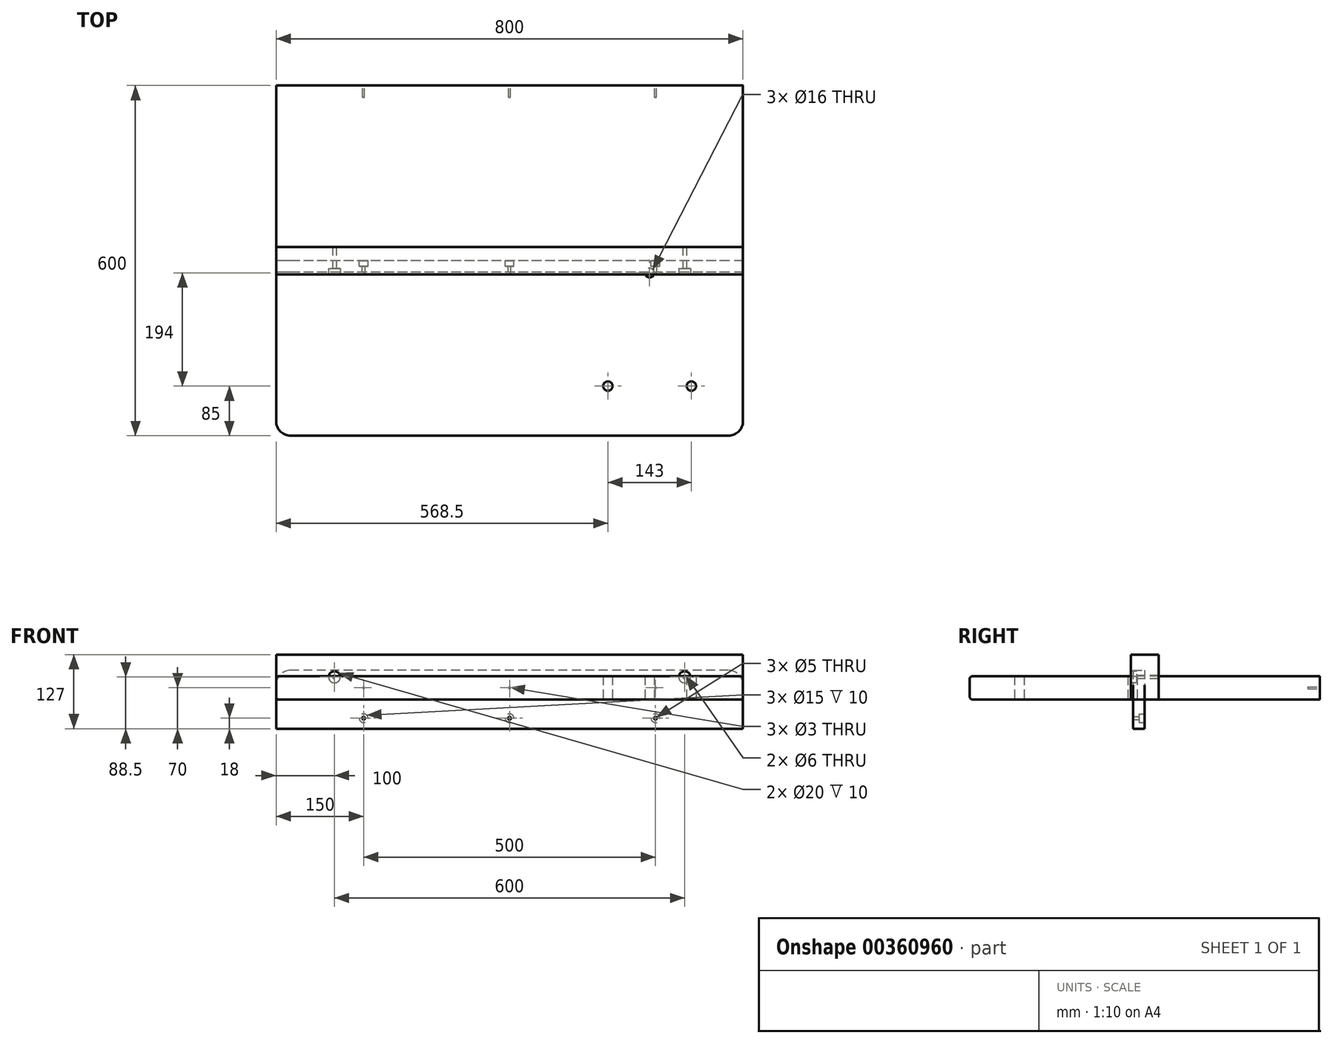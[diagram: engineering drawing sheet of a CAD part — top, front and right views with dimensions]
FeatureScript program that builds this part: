
annotation { "Feature Type Name" : "Feature", "Feature Type Description" : "" }
export const myFeature = defineFeature(function(context is Context, id is Id, definition is map)
    precondition{}
    {
        {
            var Q0;
            Q0=qCreatedBy(makeId("Top.planeOp"),FACE);
            var sketch = newSketch(context, id + "F0", { "sketchPlane" : qUnion([Q0])});
            skLineSegment(sketch, "E0.bottom", {"start": v(400, 300) * mm, "end": v(-400, 300) * mm});
            skLineSegment(sketch, "E0.top", {"start": v(400, -300) * mm, "end": v(-400, -300) * mm});
            skLineSegment(sketch, "E0.left", {"start": v(400, 300) * mm, "end": v(400, -300) * mm});
            skLineSegment(sketch, "E0.right", {"start": v(-400, 300) * mm, "end": v(-400, -300) * mm});
            skPoint(sketch, "E0.middle", {"position": v(0, 0) * mm});
            skPoint(sketch, "E1", {"position": v(240, -21) * mm});
            skPoint(sketch, "E2", {"position": v(168.5, -215) * mm});
            skPoint(sketch, "E3", {"position": v(311.5, -215) * mm});
            skLineSegment(sketch, "E4", {"start": v(311.5, -215) * mm, "end": v(168.5, -215) * mm, "construction": true});
            skLineSegment(sketch, "E5", {"start": v(240, -21) * mm, "end": v(240, -215) * mm, "construction": true});
            skSolve(sketch);
        }
        {
            var Q0;
            Q0=makeQuery(id+"F0.imprint","IMPRINT",FACE,{"disambiguationData":[TD([[makeQuery(id+"F0.imprint","IMPRINT",EDGE,{"derivedFrom":sQuery(id+"F0.wireOp",EDGE,"E0.bottom")}),1.0]])]});
            extrude(context, id + "F1", {"entities" : qUnion([Q0]), "depth" : 40 * mm, "offsetDistance" : 25 * mm});
        }
        {
            var Q0;
            Q0=makeQuery(id+"F1.opExtrude","SWEPT_EDGE",EDGE,{"disambiguationData":[OSD([sQuery(id+"F0.wireOp",EDGE,"E0.top"),sQuery(id+"F0.wireOp",EDGE,"E0.left")])]});
            var Q1;
            Q1=makeQuery(id+"F1.opExtrude","SWEPT_EDGE",EDGE,{"disambiguationData":[OSD([sQuery(id+"F0.wireOp",EDGE,"E0.top"),sQuery(id+"F0.wireOp",EDGE,"E0.right")])]});
            fillet(context, id + "F2", {"entities" : qUnion([Q0, Q1]), "radius" : 25 * mm, "tangentPropagation" : true, "allowEdgeOverflow" : false});
        }
        {
            var Q0;
            Q0=makeQuery(id+"F1.opExtrude","CAP_EDGE",EDGE,{"disambiguationData":[OSD([sQuery(id+"F0.wireOp",EDGE,"E0.left")])],"isStart":false});
            var Q1;
            Q1=makeQuery(id+"F1.opExtrude","CAP_EDGE",EDGE,{"disambiguationData":[OSD([sQuery(id+"F0.wireOp",EDGE,"E0.top")])],"isStart":true});
            fillet(context, id + "F3", {"entities" : qUnion([Q0, Q1]), "radius" : 5 * mm, "tangentPropagation" : true, "allowEdgeOverflow" : false});
        }
        {
            var Q0;
            Q0=makeQuery(id+"F1.opExtrude","SWEPT_FACE",FACE,{"disambiguationData":[OSD([sQuery(id+"F0.wireOp",EDGE,"E0.bottom")])]});
            var sketch = newSketch(context, id + "F4", { "sketchPlane" : qUnion([Q0])});
            skLineSegment(sketch, "E6", {"start": v(-400, 20) * mm, "end": v(400, 20) * mm, "construction": true});
            skPoint(sketch, "E7", {"position": v(0, 20) * mm});
            skPoint(sketch, "E8", {"position": v(-250, 20) * mm});
            skPoint(sketch, "E9", {"position": v(250, 20) * mm});
            skSolve(sketch);
        }
        {
            var Q0;
            Q0=sQuery(id+"F4.wireOp",VERTEX,"E8");
            var Q1;
            Q1=sQuery(id+"F4.wireOp",VERTEX,"E7");
            var Q2;
            Q2=sQuery(id+"F4.wireOp",VERTEX,"E9");
            var Q3;
            Q3=makeQuery(id+"F1.opExtrude","SWEPT_BODY",BODY,{"disambiguationData":[OSD([sQuery(id+"F0.wireOp",EDGE,"E0.bottom"),sQuery(id+"F0.wireOp",EDGE,"E0.top"),sQuery(id+"F0.wireOp",EDGE,"E0.left"),sQuery(id+"F0.wireOp",EDGE,"E0.right")])]});
            hole(context, id + "F5", {"style" : HoleStyle.SIMPLE, "endStyle" : HoleEndStyle.BLIND, "holeDiameter" : 3 * mm, "holeDepth" : 20 * mm, "isTappedThrough" : true, "tappedDepth" : 12 * mm, "tapClearance" : 3, "locations" : qUnion([Q0, Q1, Q2]), "scope" : qUnion([Q3])});
        }
        {
            var Q0;
            Q0=qCreatedBy(makeId("Front.planeOp"),FACE);
            var sketch = newSketch(context, id + "F6", { "sketchPlane" : qUnion([Q0])});
            skLineSegment(sketch, "E10.bottom", {"start": v(375, 50) * mm, "end": v(-375, 50) * mm});
            skLineSegment(sketch, "E10.top", {"start": v(400, -50) * mm, "end": v(-400, -50) * mm});
            skLineSegment(sketch, "E10.left", {"start": v(400, 25) * mm, "end": v(400, -50) * mm});
            skLineSegment(sketch, "E10.right", {"start": v(-400, 25) * mm, "end": v(-400, -50) * mm});
            skPoint(sketch, "E10.middle", {"position": v(0, 0) * mm});
            skLineSegment(sketch, "E11", {"start": v(-400, -32) * mm, "end": v(400, -32) * mm, "construction": true});
            skPoint(sketch, "E11.endSnap0", {"position": v(400, 0) * mm});
            skPoint(sketch, "E12", {"position": v(0, -32) * mm});
            skPoint(sketch, "E13", {"position": v(250, -32) * mm});
            skPoint(sketch, "E14", {"position": v(-250, -32) * mm});
            skPoint(sketch, "E15.visualSharp", {"position": v(-400, 50) * mm});
            skArc(sketch, "E15.filletArc", {"start": v(-375, 50) * mm, "mid": v(-392.68, 42.68) * mm, "end": v(-400, 25) * mm});
            skPoint(sketch, "E16.visualSharp", {"position": v(400, 50) * mm});
            skArc(sketch, "E16.filletArc", {"start": v(400, 25) * mm, "mid": v(392.68, 42.68) * mm, "end": v(375, 50) * mm});
            skSolve(sketch);
        }
        {
            var Q0;
            Q0=makeQuery(id+"F6.imprint","IMPRINT",FACE,{"disambiguationData":[TD([[makeQuery(id+"F6.imprint","IMPRINT",EDGE,{"derivedFrom":sQuery(id+"F6.wireOp",EDGE,"E10.bottom")}),1.0]])]});
            extrude(context, id + "F7", {"entities" : qUnion([Q0]), "depth" : 20 * mm});
        }
        {
            var Q0;
            Q0=sQuery(id+"F6.wireOp",VERTEX,"E13");
            var Q1;
            Q1=sQuery(id+"F6.wireOp",VERTEX,"E12");
            var Q2;
            Q2=sQuery(id+"F6.wireOp",VERTEX,"E14");
            var Q3;
            Q3=makeQuery(id+"F7.opExtrude","SWEPT_BODY",BODY,{"disambiguationData":[OSD([sQuery(id+"F6.wireOp",EDGE,"E10.bottom"),sQuery(id+"F6.wireOp",EDGE,"E10.top"),sQuery(id+"F6.wireOp",EDGE,"E10.left"),sQuery(id+"F6.wireOp",EDGE,"E10.right"),sQuery(id+"F6.wireOp",EDGE,"E15.filletArc"),sQuery(id+"F6.wireOp",EDGE,"E16.filletArc")])]});
            hole(context, id + "F8", {"style" : HoleStyle.C_BORE, "endStyle" : HoleEndStyle.THROUGH, "oppositeDirection" : true, "holeDiameter" : 5 * mm, "cBoreDiameter" : 15 * mm, "cBoreDepth" : 10 * mm, "isTappedThrough" : true, "tappedDepth" : 12 * mm, "tapClearance" : 3, "locations" : qUnion([Q0, Q1, Q2]), "scope" : qUnion([Q3])});
        }
        {
            var Q0;
            Q0=qCreatedBy(makeId("Top.planeOp"),FACE);
            var sketch = newSketch(context, id + "F9", { "sketchPlane" : qUnion([Q0])});
            skLineSegment(sketch, "E17.bottom", {"start": v(400, 23.5) * mm, "end": v(-400, 23.5) * mm});
            skLineSegment(sketch, "E17.top", {"start": v(400, -23.5) * mm, "end": v(-400, -23.5) * mm});
            skLineSegment(sketch, "E17.left", {"start": v(400, 23.5) * mm, "end": v(400, -23.5) * mm});
            skLineSegment(sketch, "E17.right", {"start": v(-400, 23.5) * mm, "end": v(-400, -23.5) * mm});
            skPoint(sketch, "E17.middle", {"position": v(0, 0) * mm});
            skSolve(sketch);
        }
        {
            var Q0;
            Q0=makeQuery(id+"F9.imprint","IMPRINT",FACE,{"disambiguationData":[TD([[makeQuery(id+"F9.imprint","IMPRINT",EDGE,{"derivedFrom":sQuery(id+"F9.wireOp",EDGE,"E17.bottom")}),1.0]])]});
            extrude(context, id + "F10", {"entities" : qUnion([Q0]), "depth" : 77 * mm});
        }
        {
            var Q0;
            Q0=makeQuery(id+"F10.opExtrude","SWEPT_FACE",FACE,{"disambiguationData":[OSD([sQuery(id+"F9.wireOp",EDGE,"E17.top")])]});
            var sketch = newSketch(context, id + "F11", { "sketchPlane" : qUnion([Q0])});
            skLineSegment(sketch, "E18", {"start": v(-400, 38.5) * mm, "end": v(400, 38.5) * mm});
            skPoint(sketch, "E19", {"position": v(300, 38.5) * mm});
            skPoint(sketch, "E20", {"position": v(-300, 38.5) * mm});
            skSolve(sketch);
        }
        {
            var Q0;
            Q0=sQuery(id+"F11.wireOp",VERTEX,"E20");
            var Q1;
            Q1=sQuery(id+"F11.wireOp",VERTEX,"E19");
            var Q2;
            Q2=makeQuery(id+"F10.opExtrude","SWEPT_BODY",BODY,{"disambiguationData":[OSD([sQuery(id+"F9.wireOp",EDGE,"E17.bottom"),sQuery(id+"F9.wireOp",EDGE,"E17.top"),sQuery(id+"F9.wireOp",EDGE,"E17.left"),sQuery(id+"F9.wireOp",EDGE,"E17.right")])]});
            hole(context, id + "F12", {"style" : HoleStyle.C_BORE, "endStyle" : HoleEndStyle.THROUGH, "holeDiameter" : 6 * mm, "cBoreDiameter" : 20 * mm, "cBoreDepth" : 10 * mm, "isTappedThrough" : true, "tappedDepth" : 12 * mm, "tapClearance" : 3, "locations" : qUnion([Q0, Q1]), "scope" : qUnion([Q2])});
        }
        {
            var Q0;
            Q0=sQuery(id+"F0.wireOp",VERTEX,"E2");
            var Q1;
            Q1=sQuery(id+"F0.wireOp",VERTEX,"E3");
            var Q2;
            Q2=sQuery(id+"F0.wireOp",VERTEX,"E1");
            var Q3;
            Q3=makeQuery(id+"F1.opExtrude","SWEPT_BODY",BODY,{"disambiguationData":[OSD([sQuery(id+"F0.wireOp",EDGE,"E0.bottom"),sQuery(id+"F0.wireOp",EDGE,"E0.top"),sQuery(id+"F0.wireOp",EDGE,"E0.left"),sQuery(id+"F0.wireOp",EDGE,"E0.right")])]});
            hole(context, id + "F13", {"style" : HoleStyle.SIMPLE, "endStyle" : HoleEndStyle.THROUGH, "oppositeDirection" : true, "standardTappedOrClearance" : lookupTablePath({ "standard" : "ISO", "size" : "16", "type" : "Drilled" }), "standardBlindInLast" : lookupTablePath({ "standard" : "ISO", "size" : "16", "type" : "Drilled" }), "holeDiameter" : 16 * mm, "majorDiameter" : 16 * mm, "isTappedThrough" : true, "tappedDepth" : 12 * mm, "tapClearance" : 3, "locations" : qUnion([Q0, Q1, Q2]), "scope" : qUnion([Q3])});
        }
    });
